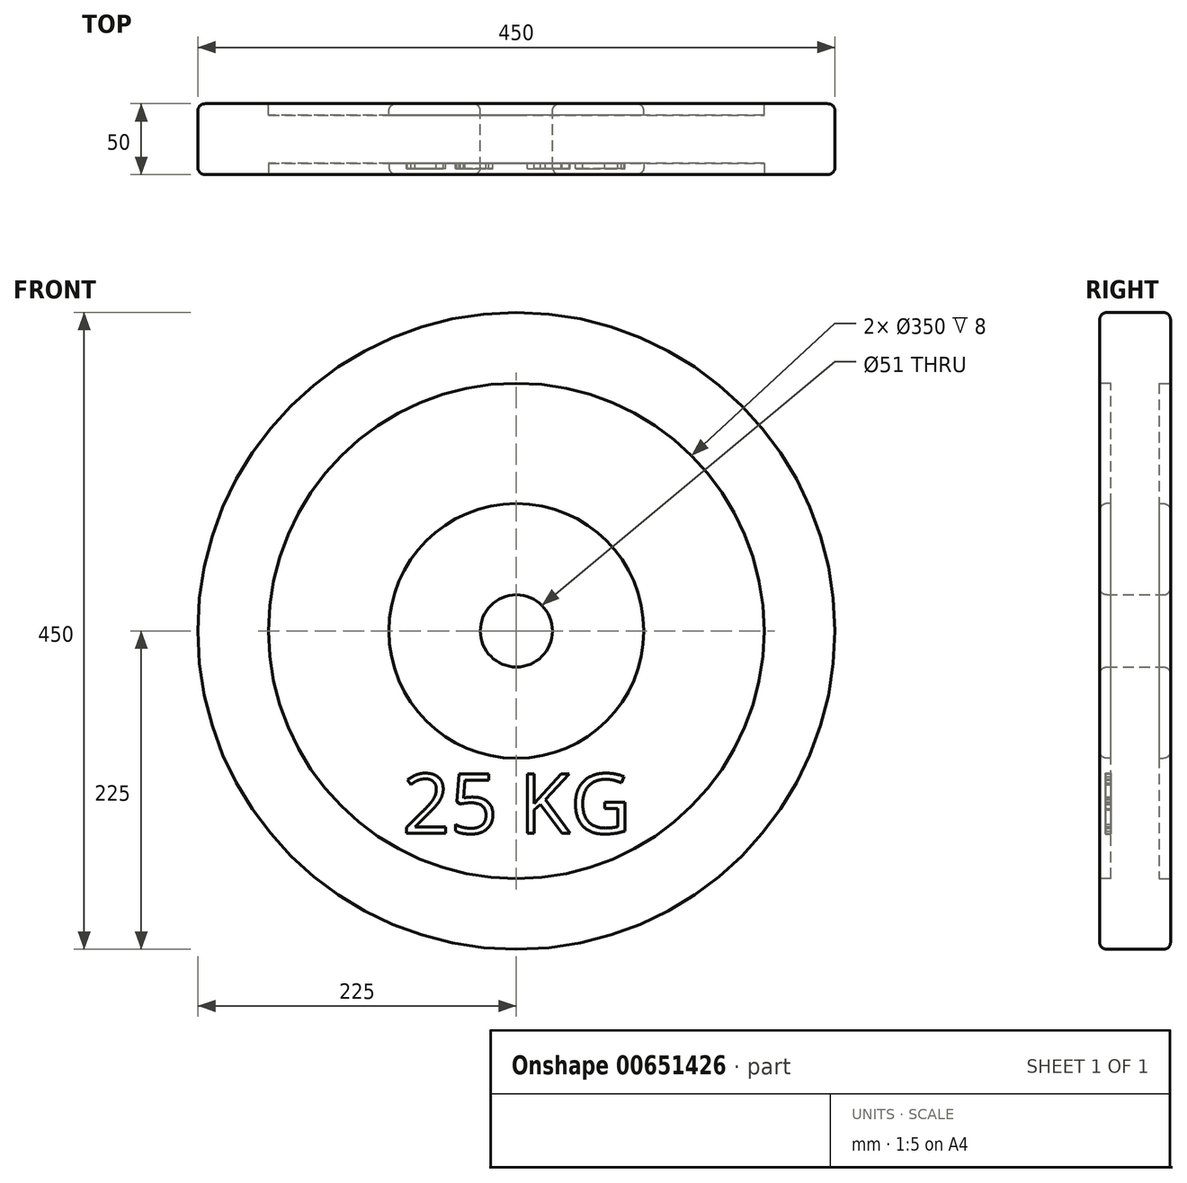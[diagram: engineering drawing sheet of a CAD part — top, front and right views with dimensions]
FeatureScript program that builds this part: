
annotation { "Feature Type Name" : "Feature", "Feature Type Description" : "" }
export const myFeature = defineFeature(function(context is Context, id is Id, definition is map)
    precondition{}
    {
        {
            var Q0;
            Q0=qCreatedBy(makeId("Front.planeOp"),FACE);
            var sketch = newSketch(context, id + "F0", { "sketchPlane" : qUnion([Q0])});
            skCircle(sketch, "E0", {"center": v(0, 0) * mm, "radius": 25.5 * mm});
            skCircle(sketch, "E1", {"center": v(0, 0) * mm, "radius": 225 * mm});
            skSolve(sketch);
        }
        {
            var Q0;
            Q0 = qSketchRegion(id + "F0", true);
            extrude(context, id + "F1", {"entities" : qUnion([Q0]), "depth" : 50 * mm, "offsetDistance" : 25 * mm});
        }
        {
            var Q0;
            Q0=makeQuery(id+"F1.opExtrude","CAP_FACE",FACE,{"disambiguationData":[OSD([sQuery(id+"F0.wireOp",EDGE,"E0"),sQuery(id+"F0.wireOp",EDGE,"E1")])],"isStart":false});
            var Q1;
            Q1=makeQuery(id+"F1.opExtrude","CAP_FACE",FACE,{"disambiguationData":[OSD([sQuery(id+"F0.wireOp",EDGE,"E0"),sQuery(id+"F0.wireOp",EDGE,"E1")])],"isStart":true});
            fillet(context, id + "F2", {"entities" : qUnion([Q0, Q1]), "radius" : 5 * mm, "tangentPropagation" : true, "allowEdgeOverflow" : false});
        }
        {
            var Q0;
            Q0=makeQuery(id+"F1.opExtrude","CAP_FACE",FACE,{"disambiguationData":[OSD([sQuery(id+"F0.wireOp",EDGE,"E0"),sQuery(id+"F0.wireOp",EDGE,"E1")])],"isStart":true});
            var sketch = newSketch(context, id + "F3", { "sketchPlane" : qUnion([Q0])});
            skCircle(sketch, "E2", {"center": v(0, 0) * mm, "radius": 90 * mm});
            skCircle(sketch, "E3", {"center": v(0, 0) * mm, "radius": 175 * mm});
            skSolve(sketch);
        }
        {
            var Q0;
            Q0 = qSketchRegion(id + "F3", true);
            extrude(context, id + "F4", {"entities" : qUnion([Q0]), "operationType" : NewBodyOperationType.REMOVE, "oppositeDirection" : true, "depth" : 8 * mm, "offsetDistance" : 25 * mm});
        }
        {
            var Q0;
            Q0=makeQuery(id+"F1.opExtrude","CAP_FACE",FACE,{"disambiguationData":[OSD([sQuery(id+"F0.wireOp",EDGE,"E0"),sQuery(id+"F0.wireOp",EDGE,"E1")])],"isStart":false});
            var sketch = newSketch(context, id + "F5", { "sketchPlane" : qUnion([Q0])});
            skCircle(sketch, "E4", {"center": v(0, 0) * mm, "radius": 90 * mm});
            skCircle(sketch, "E5", {"center": v(0, 0) * mm, "radius": 175 * mm});
            skSolve(sketch);
        }
        {
            var Q0;
            Q0 = qSketchRegion(id + "F5", true);
            extrude(context, id + "F6", {"entities" : qUnion([Q0]), "operationType" : NewBodyOperationType.REMOVE, "oppositeDirection" : true, "depth" : 8 * mm, "offsetDistance" : 25 * mm});
        }
        {
            var Q0;
            {var subQ0=sQuery(id+"F0.wireOp",EDGE,"E0");Q0=makeQuery(id+"F6.boolean.opBoolean","SPLIT",FACE,{"disambiguationData":[TD([makeQuery(id+"F6.opExtrude","SWEPT_FACE",FACE,{"disambiguationData":[OSD([sQuery(id+"F5.wireOp",EDGE,"E4")])]})])],"derivedFrom":makeQuery(id+"F1.opExtrude","CAP_FACE",FACE,{"disambiguationData":[OSD([subQ0,sQuery(id+"F0.wireOp",EDGE,"E1")])],"isStart":false})});}
            var Q1;
            Q1=makeQuery(id+"F6.boolean.opBoolean","COPY",EDGE,{"derivedFrom":makeQuery(id+"F6.opExtrude","CAP_EDGE",EDGE,{"disambiguationData":[OSD([sQuery(id+"F5.wireOp",EDGE,"E5")])],"isStart":true})});
            var Q2;
            Q2=makeQuery(id+"F4.boolean.opBoolean","COPY",EDGE,{"derivedFrom":makeQuery(id+"F4.opExtrude","CAP_EDGE",EDGE,{"disambiguationData":[OSD([sQuery(id+"F3.wireOp",EDGE,"E3")])],"isStart":true})});
            var Q3;
            Q3=makeQuery(id+"F4.boolean.opBoolean","COPY",EDGE,{"derivedFrom":makeQuery(id+"F4.opExtrude","CAP_EDGE",EDGE,{"disambiguationData":[OSD([sQuery(id+"F3.wireOp",EDGE,"E2")])],"isStart":true})});
            fillet(context, id + "F7", {"entities" : qUnion([Q0, Q1, Q2, Q3]), "radius" : 5 * mm, "tangentPropagation" : true, "allowEdgeOverflow" : false});
        }
        {
            var Q0;
            Q0=makeQuery(id+"F6.boolean.opBoolean","COPY",FACE,{"derivedFrom":makeQuery(id+"F6.opExtrude","CAP_FACE",FACE,{"disambiguationData":[OSD([sQuery(id+"F5.wireOp",EDGE,"E4"),sQuery(id+"F5.wireOp",EDGE,"E5")])],"isStart":false})});
            var sketch = newSketch(context, id + "F8", { "sketchPlane" : qUnion([Q0])});
            skText(sketch, "E6", { "text": "25 KG", "fontName": "OpenSans-Regular.ttf"});
            const initialGuessF8  = {"E6": [-0.08035, -0.14301, 1, 0, 0.04228]};
            skSetInitialGuess(sketch, initialGuessF8);
            skSolve(sketch);
        }
        {
            var Q0;
            Q0 = qSketchRegion(id + "F8", true);
            extrude(context, id + "F9", {"entities" : qUnion([Q0]), "depth" : 4 * mm, "offsetDistance" : 25 * mm});
        }
    });
